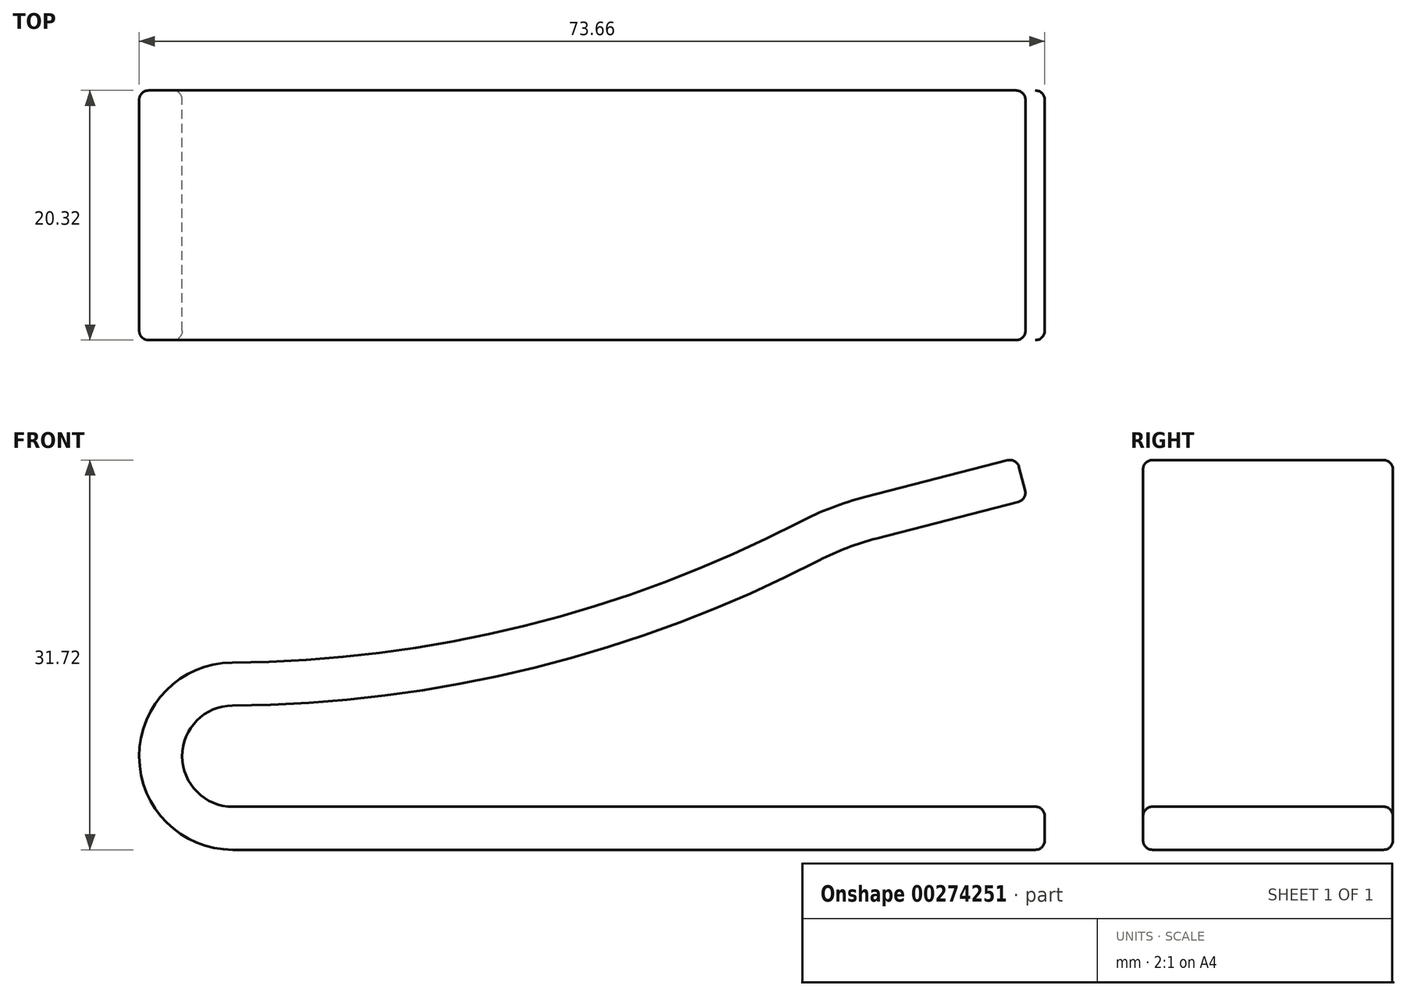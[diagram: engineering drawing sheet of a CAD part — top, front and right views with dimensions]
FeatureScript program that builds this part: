
annotation { "Feature Type Name" : "Feature", "Feature Type Description" : "" }
export const myFeature = defineFeature(function(context is Context, id is Id, definition is map)
    precondition{}
    {
        {
            var Q0;
            Q0=qCreatedBy(makeId("Front.planeOp"),FACE);
            var sketch = newSketch(context, id + "F0", { "sketchPlane" : qUnion([Q0])});
            skLineSegment(sketch, "E0", {"start": v(33.76, 0) * mm, "end": v(-32.28, 0) * mm});
            skArc(sketch, "E1", {"start": v(-32.33, 15.24) * mm, "mid": v(-39.9, 7.6) * mm, "end": v(-32.28, 0) * mm});
            skArc(sketch, "E2", {"start": v(-32.33, 15.24) * mm, "mid": v(-8.59, 18.22) * mm, "end": v(13.8, 26.66) * mm});
            skLineSegment(sketch, "E3", {"start": v(19.18, 28.72) * mm, "end": v(31.48, 31.88) * mm});
            skPoint(sketch, "E4.visualSharp", {"position": v(16.22, 27.96) * mm});
            skArc(sketch, "E4.filletArc", {"start": v(19.18, 28.72) * mm, "mid": v(16.43, 27.84) * mm, "end": v(13.8, 26.66) * mm});
            skLineSegment(sketch, "E5", {"start": v(31.48, 31.88) * mm, "end": v(-47.44, 11.59) * mm, "construction": true});
            skLineSegment(sketch, "E6.0", {"start": v(20.05, 25.33) * mm, "end": v(32.35, 28.5) * mm});
            skLineSegment(sketch, "E6.1", {"start": v(33.76, 3.5) * mm, "end": v(-32.28, 3.5) * mm});
            skArc(sketch, "E6.2", {"start": v(-32.3, 11.74) * mm, "mid": v(-36.4, 7.6) * mm, "end": v(-32.28, 3.5) * mm});
            skArc(sketch, "E6.3", {"start": v(-32.3, 11.74) * mm, "mid": v(-7.75, 14.82) * mm, "end": v(15.42, 23.56) * mm});
            skArc(sketch, "E6.4", {"start": v(20.05, 25.33) * mm, "mid": v(17.68, 24.58) * mm, "end": v(15.42, 23.56) * mm});
            skLineSegment(sketch, "E7", {"start": v(-47.44, 7.57) * mm, "end": v(92.85, 8.04) * mm, "construction": true});
            skArc(sketch, "E8.MirrorCS", {"start": v(-32.28, 3.5) * mm, "mid": v(-7.7, 0.58) * mm, "end": v(15.52, -8) * mm, "construction": true});
            skArc(sketch, "E9.MirrorCS", {"start": v(-32.28, 0) * mm, "mid": v(-8.52, -2.82) * mm, "end": v(13.93, -11.12) * mm, "construction": true});
            skArc(sketch, "E10.MirrorCS", {"start": v(20.17, -9.74) * mm, "mid": v(17.8, -9) * mm, "end": v(15.52, -8) * mm, "construction": true});
            skArc(sketch, "E11.MirrorCS", {"start": v(19.32, -13.14) * mm, "mid": v(16.57, -12.28) * mm, "end": v(13.93, -11.12) * mm, "construction": true});
            skLineSegment(sketch, "E12.MirrorCS", {"start": v(31.64, -16.22) * mm, "end": v(-47.42, 3.55) * mm, "construction": true});
            skLineSegment(sketch, "E13.MirrorCS", {"start": v(20.17, -9.74) * mm, "end": v(32.5, -12.82) * mm, "construction": true});
            skLineSegment(sketch, "E14.MirrorCS", {"start": v(19.32, -13.14) * mm, "end": v(31.64, -16.22) * mm, "construction": true});
            skLineSegment(sketch, "E15", {"start": v(31.64, -16.22) * mm, "end": v(32.5, -12.82) * mm, "construction": true});
            skLineSegment(sketch, "E16", {"start": v(31.48, 31.88) * mm, "end": v(32.35, 28.5) * mm});
            skLineSegment(sketch, "E17", {"start": v(33.76, 3.5) * mm, "end": v(33.76, 0) * mm});
            skSolve(sketch);
        }
        {
            var Q0;
            Q0=makeQuery(id+"F0.imprint","IMPRINT",FACE,{"disambiguationData":[TD([[makeQuery(id+"F0.imprint","IMPRINT",EDGE,{"derivedFrom":sQuery(id+"F0.wireOp",EDGE,"E1")}),1.0]])]});
            extrude(context, id + "F1", {"entities" : qUnion([Q0]), "depth" : 20.32 * mm});
        }
        {
            var Q0;
            Q0=makeQuery(id+"F1.opExtrude","CAP_FACE",FACE,{"disambiguationData":[OSD([sQuery(id+"F0.wireOp",EDGE,"E1"),sQuery(id+"F0.wireOp",EDGE,"E2"),sQuery(id+"F0.wireOp",EDGE,"E3"),sQuery(id+"F0.wireOp",EDGE,"E4.filletArc"),sQuery(id+"F0.wireOp",EDGE,"E6.0"),sQuery(id+"F0.wireOp",EDGE,"E6.2"),sQuery(id+"F0.wireOp",EDGE,"E6.3"),sQuery(id+"F0.wireOp",EDGE,"E6.4"),sQuery(id+"F0.wireOp",EDGE,"E8.MirrorCS"),sQuery(id+"F0.wireOp",EDGE,"E9.MirrorCS"),sQuery(id+"F0.wireOp",EDGE,"E10.MirrorCS"),sQuery(id+"F0.wireOp",EDGE,"E11.MirrorCS"),sQuery(id+"F0.wireOp",EDGE,"E13.MirrorCS"),sQuery(id+"F0.wireOp",EDGE,"E14.MirrorCS"),sQuery(id+"F0.wireOp",EDGE,"E15"),sQuery(id+"F0.wireOp",EDGE,"E16")])],"isStart":false});
            var Q1;
            Q1=makeQuery(id+"F1.opExtrude","CAP_FACE",FACE,{"disambiguationData":[OSD([sQuery(id+"F0.wireOp",EDGE,"E1"),sQuery(id+"F0.wireOp",EDGE,"E2"),sQuery(id+"F0.wireOp",EDGE,"E3"),sQuery(id+"F0.wireOp",EDGE,"E4.filletArc"),sQuery(id+"F0.wireOp",EDGE,"E6.0"),sQuery(id+"F0.wireOp",EDGE,"E6.2"),sQuery(id+"F0.wireOp",EDGE,"E6.3"),sQuery(id+"F0.wireOp",EDGE,"E6.4"),sQuery(id+"F0.wireOp",EDGE,"E8.MirrorCS"),sQuery(id+"F0.wireOp",EDGE,"E9.MirrorCS"),sQuery(id+"F0.wireOp",EDGE,"E10.MirrorCS"),sQuery(id+"F0.wireOp",EDGE,"E11.MirrorCS"),sQuery(id+"F0.wireOp",EDGE,"E13.MirrorCS"),sQuery(id+"F0.wireOp",EDGE,"E14.MirrorCS"),sQuery(id+"F0.wireOp",EDGE,"E15"),sQuery(id+"F0.wireOp",EDGE,"E16")])],"isStart":true});
            var Q2;
            Q2=makeQuery(id+"F1.opExtrude","SWEPT_FACE",FACE,{"disambiguationData":[OSD([sQuery(id+"F0.wireOp",EDGE,"E16")])]});
            var Q3;
            Q3=makeQuery(id+"F1.opExtrude","SWEPT_FACE",FACE,{"disambiguationData":[OSD([sQuery(id+"F0.wireOp",EDGE,"E15")])]});
            var Q4;
            Q4=makeQuery(id+"F1.opExtrude","SWEPT_FACE",FACE,{"disambiguationData":[OSD([sQuery(id+"F0.wireOp",EDGE,"E17")])]});
            fillet(context, id + "F2", {"entities" : qUnion([Q0, Q1, Q2, Q3, Q4]), "radius" : 0.76 * mm, "tangentPropagation" : true, "allowEdgeOverflow" : false});
        }
    });
